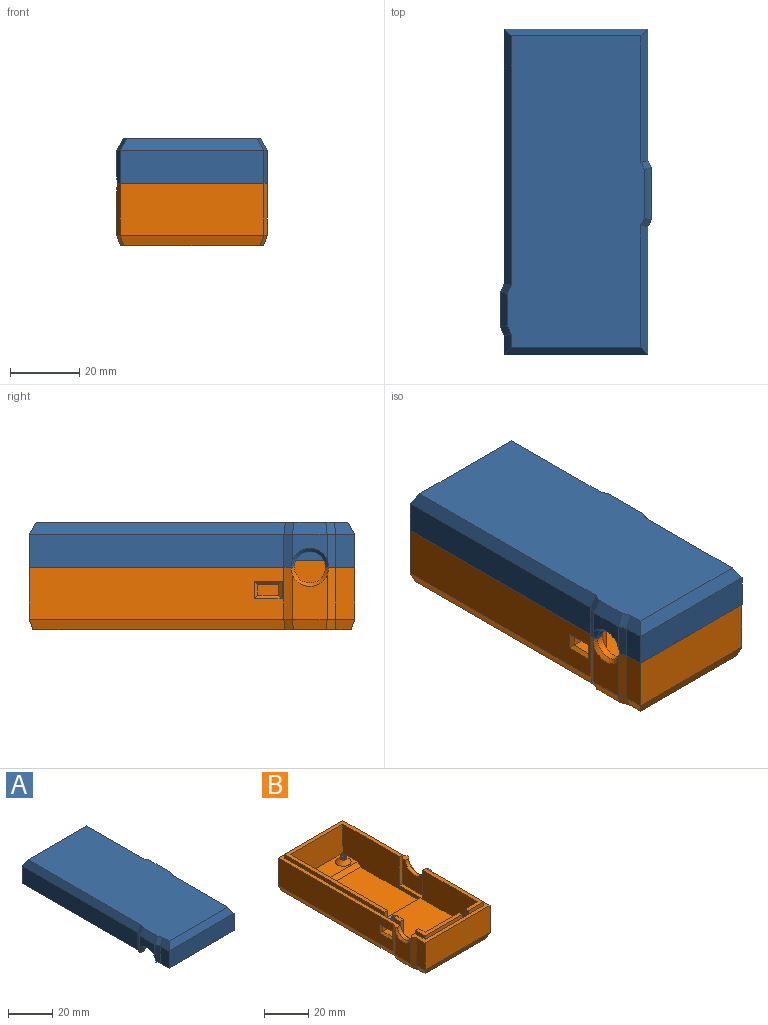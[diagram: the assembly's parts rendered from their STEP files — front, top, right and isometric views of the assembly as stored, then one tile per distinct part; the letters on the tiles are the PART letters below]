
ASSEMBLY  parts=2 mates=1
PART A: 69 faces, bbox 43.6x94.1x20.1 mm
  f0: plane 88x37.5mm, normal (0,0,-1), area 2730.7mm2, adj f15,f16,f17,f18,f19,f20,f21,f22
  f1: plane 37.5x6.43mm, normal (0,-1,0), area 110.4mm2, adj f2,f19,f23,f25,f29,f36,f37,f49
  f2: plane 76.5x43.36mm, normal (0,0,-1), area 315.8mm2, adj f1,f4,f6,f7,f8,f9,f10,f19
  f3: plane 10x7.24mm, normal (-1,0,0), area 49.4mm2, adj f10,f11,f62,f64
  f4: plane 15x9.54mm, normal (1,0,0), area 76.7mm2, adj f2,f5,f6,f31,f53,f68
  f5: plane 43.36x41mm, normal (0,0,-1), area 177.8mm2, adj f4,f11,f12,f13,f14,f19,f29,f31
  f6: plane 9.54x2mm, normal (0.89,0.45,0), area 21.3mm2, adj f2,f4,f7,f55
  f7: plane 38x9.54mm, normal (1,0,0), area 362.4mm2, adj f2,f6,f8,f57
  f8: plane 41.5x9.54mm, normal (0,1,0), area 354.7mm2, adj f2,f7,f9,f59,f65,f66,f67
  f9: plane 73.53x9.54mm, normal (-1,0,0), area 701.2mm2, adj f2,f8,f10,f61
  f10: plane 9.64x2.57mm, normal (-0.93,0.38,0), area 24.8mm2, adj f2,f3,f9,f63,f64
  f11: plane 9.64x2.57mm, normal (-0.93,-0.38,0), area 24.8mm2, adj f3,f5,f12,f60,f64
  f12: plane 9.54x5.53mm, normal (-1,0,0), area 52.7mm2, adj f5,f11,f13,f58
  f13: plane 41.5x9.54mm, normal (0,-1,0), area 395.7mm2, adj f5,f12,f14,f56
  f14: plane 37x9.54mm, normal (1,0,0), area 352.8mm2, adj f5,f13,f31,f54
  f15: plane 35x9mm, normal (-1,0,0), area 315mm2, adj f0,f16,f30,f35
  f16: plane 33.5x9mm, normal (0,1,0), area 301.5mm2, adj f0,f15,f17,f35
  f17: plane 9x4mm, normal (1,0,0), area 36mm2, adj f0,f16,f18,f35
  f18: plane 9x2mm, normal (0,1,0), area 18mm2, adj f0,f17,f19,f35
  f19: plane 90x11mm, normal (1,0,0), area 238.2mm2, adj f0,f1,f2,f5,f18,f20,f34,f35
  f20: plane 9x2mm, normal (0,-1,0), area 18mm2, adj f0,f19,f21,f37
  f21: plane 72x9mm, normal (1,0,0), area 648mm2, adj f0,f20,f22,f37
  f22: plane 9x7.75mm, normal (0,-1,0), area 69.8mm2, adj f0,f21,f23,f37
  f23: plane 9x3mm, normal (1,0,0), area 21.1mm2, adj f0,f1,f22,f24,f37,f48,f49,f65
  f24: plane 8x1.43mm, normal (0,-1,0), area 11.4mm2, adj f0,f23,f25,f48
  f25: plane 9x3mm, normal (-1,0,0), area 21.1mm2, adj f0,f1,f24,f26,f36,f48,f49,f67
  f26: plane 17.75x9mm, normal (0,-1,0), area 155.4mm2, adj f0,f25,f27,f32,f36,f51
  f27: plane 36x9mm, normal (-1,0,0), area 318mm2, adj f0,f26,f28,f32,f36,f51
  f28: plane 9x2mm, normal (0,-1,0), area 18mm2, adj f0,f27,f29,f36
  f29: plane 90x11mm, normal (-1,0,0), area 267.5mm2, adj f0,f1,f2,f5,f28,f30,f34,f35
  f30: plane 9x2mm, normal (0,1,0), area 18mm2, adj f0,f15,f29,f35
  f31: plane 9.54x2mm, normal (0.89,-0.45,0), area 21.3mm2, adj f4,f5,f14,f52
  f32: plane 1.43x1.33mm, normal (0,0,-1), area 0.9mm2, adj f26,f27,f51
  f33: plane 90x39.5mm, normal (0,0,1), area 3402.7mm2, adj f52,f53,f54,f55,f56,f57,f58,f59
  f34: plane 37.5x2mm, normal (0,1,0), area 75mm2, adj f5,f19,f29,f35
  f35: plane 37.5x37mm, normal (0,0,-1), area 153mm2, adj f15,f16,f17,f18,f19,f29,f30,f34
  f36: plane 38x19.75mm, normal (0,0,-1), area 111.5mm2, adj f1,f25,f26,f27,f28,f29
  f37: plane 74x9.75mm, normal (0,0,-1), area 163.5mm2, adj f1,f19,f20,f21,f22,f23
  f38: cylinder r=1mm len=18mm, axis (0,0,1), area 113.1mm2, adj f40,f41
  f39: cylinder r=3mm len=15mm, axis (0,0,1), area 282.7mm2, adj f40,f51
  f40: plane 6x6mm, normal (0,0,-1), area 25.1mm2, adj f38,f39
  f41: plane 2x2mm, normal (0,0,-1), area 3.1mm2, adj f38
  f42: cylinder r=1mm len=18mm, axis (0,0,1), area 113.1mm2, adj f44,f45
  f43: cylinder r=3mm len=15mm, axis (0,0,1), area 282.7mm2, adj f44,f50
  f44: plane 6x6mm, normal (0,0,-1), area 25.1mm2, adj f42,f43
  f45: plane 2x2mm, normal (0,0,-1), area 3.1mm2, adj f42
  f46: cylinder r=5.5mm len=11mm, axis (1,0,0), area 34.6mm2, adj f2,f5,f29,f68
  f47: cylinder r=4.5mm len=9mm, axis (-1,0,0), area 28.3mm2, adj f2,f5,f19,f64
  f48: plane 9.96x1.98mm, normal (0,0,-1), area 16.8mm2, adj f23,f24,f25,f59,f65,f67
  f49: plane 8x1mm, normal (0,0,1), area 8mm2, adj f1,f23,f25,f66
  f50: cone r=6mm half-angle=45deg, axis (0,0,1), area 120mm2, adj f0,f43
  f51: cone r=6mm half-angle=45deg, axis (0,0,1), area 104.8mm2, adj f0,f26,f27,f32,f39
  f52: plane 3.46x3mm, normal (0.77,-0.39,0.5), area 8.9mm2, adj f31,f33,f53,f54
  f53: plane 15x3.46mm, normal (0.87,0,0.5), area 58.1mm2, adj f4,f33,f52,f55
  f54: plane 37.47x3.46mm, normal (0.87,0,0.5), area 144.9mm2, adj f14,f33,f52,f56
  f55: plane 3.46x3mm, normal (0.77,0.39,0.5), area 8.9mm2, adj f6,f33,f53,f57
  f56: plane 41.5x3.46mm, normal (0,-0.87,0.5), area 158mm2, adj f13,f33,f54,f58
  f57: plane 38.47x3.46mm, normal (0.87,0,0.5), area 148.9mm2, adj f7,f33,f55,f59
  f58: plane 5.92x3.46mm, normal (-0.87,0,0.5), area 18.9mm2, adj f12,f33,f56,f60
  f59: plane 41.5x3.46mm, normal (0,0.87,0.5), area 157.6mm2, adj f8,f33,f48,f57,f61,f65,f67
  f60: plane 3.46x3mm, normal (-0.8,-0.32,0.5), area 10.7mm2, adj f11,f33,f58,f62
  f61: plane 73.92x3.46mm, normal (-0.87,0,0.5), area 290.9mm2, adj f9,f33,f59,f63
  f62: plane 10x3.46mm, normal (-0.87,0,0.5), area 38.4mm2, adj f3,f33,f60,f63
  f63: plane 3.46x3mm, normal (-0.8,0.32,0.5), area 10.7mm2, adj f10,f33,f61,f62
  f64: cone r=4.5mm half-angle=45deg, axis (-1,0,0), area 21.7mm2, adj f2,f3,f5,f10,f11,f47
  f65: plane 4.14x1mm, normal (0.71,0.71,0), area 5.2mm2, adj f8,f23,f48,f59,f66
  f66: plane 10x1mm, normal (0,0.71,0.71), area 12.7mm2, adj f8,f49,f65,f67
  f67: plane 4.14x1mm, normal (-0.71,0.71,0), area 5.2mm2, adj f8,f25,f48,f59,f66
  f68: cone r=5.5mm half-angle=45deg, axis (1,0,0), area 26.7mm2, adj f2,f4,f5,f46
PART B: 84 faces, bbox 43.5x94x20 mm
  f0: plane 35x16mm, normal (-1,0,0), area 560mm2, adj f9,f12,f13,f42
  f1: plane 4x2mm, normal (-1,0,0), area 8mm2, adj f2,f5,f21,f58
  f2: plane 4x2mm, normal (0,0,1), area 8mm2, adj f1,f3,f21,f58
  f3: plane 72x18mm, normal (1,0,0), area 1168mm2, adj f2,f7,f9,f21,f22,f39,f52,f56
  f4: plane 73.53x15mm, normal (-1,0,0), area 1062.9mm2, adj f5,f30,f31,f71,f72,f73,f74,f75
  f5: plane 76.5x43.36mm, normal (0,0,1), area 315.8mm2, adj f1,f4,f11,f20,f27,f28,f29,f30
  f6: plane 12.71x10mm, normal (-1,0,0), area 104mm2, adj f31,f32,f67,f77
  f7: plane 33.5x9.44mm, normal (0,0,1), area 277.6mm2, adj f3,f22,f23,f79,f81
  f8: plane 15x2mm, normal (0,0,1), area 30mm2, adj f9,f11,f12,f23,f34
  f9: plane 38.51x35.5mm, normal (0,0,1), area 1212.8mm2, adj f0,f3,f8,f13,f14,f15,f16,f17
  f10: plane 43.36x41mm, normal (0,0,1), area 177.8mm2, adj f11,f15,f20,f24,f25,f26,f27,f32
  f11: plane 15x14mm, normal (-1,0,0), area 162.5mm2, adj f5,f8,f10,f12,f34,f53
  f12: plane 16x2mm, normal (0,1,0), area 32mm2, adj f0,f8,f11,f41,f42
  f13: plane 16x7.72mm, normal (0,1,0), area 123.6mm2, adj f0,f9,f14,f42
  f14: plane 16x2mm, normal (-1,0,0), area 32mm2, adj f9,f13,f15,f40,f42
  f15: plane 14x4mm, normal (0,1,0), area 56mm2, adj f9,f10,f14,f16
  f16: plane 16x2mm, normal (1,0,0), area 32mm2, adj f9,f15,f17,f43,f45
  f17: plane 21.78x16mm, normal (0,1,0), area 348.4mm2, adj f9,f16,f18,f45
  f18: plane 16x4mm, normal (1,0,0), area 64mm2, adj f9,f17,f19,f45
  f19: plane 16x2mm, normal (0,1,0), area 32mm2, adj f9,f18,f20,f44,f45
  f20: plane 14x10mm, normal (1,0,0), area 108.2mm2, adj f5,f9,f10,f19,f21,f54
  f21: plane 16x2mm, normal (0,-1,0), area 32mm2, adj f1,f2,f3,f9,f20
  f22: plane 33.5x16mm, normal (0,-1,0), area 536mm2, adj f3,f7,f23,f39
  f23: plane 49.49x18mm, normal (-1,0,0), area 652.1mm2, adj f7,f8,f22,f34,f39,f52,f78,f79
  f24: plane 41.5x15mm, normal (0,-1,0), area 622.5mm2, adj f10,f25,f33,f61
  f25: plane 37x15mm, normal (1,0,0), area 555mm2, adj f10,f24,f26,f60
  f26: plane 15x2mm, normal (0.89,-0.45,0), area 33.5mm2, adj f10,f25,f27,f62
  f27: plane 15x15mm, normal (1,0,0), area 158.6mm2, adj f5,f10,f26,f28,f64,f76
  f28: plane 15x2mm, normal (0.89,0.45,0), area 33.5mm2, adj f5,f27,f29,f66
  f29: plane 38x15mm, normal (1,0,0), area 570mm2, adj f5,f28,f30,f68
  f30: plane 41.5x15mm, normal (0,1,0), area 622.5mm2, adj f4,f5,f29,f70
  f31: plane 15x2.47mm, normal (-0.93,0.38,0), area 39.4mm2, adj f4,f5,f6,f69,f77
  f32: plane 15x2.47mm, normal (-0.93,-0.38,0), area 39.4mm2, adj f6,f10,f33,f65,f77
  f33: plane 15x5.53mm, normal (-1,0,0), area 82.9mm2, adj f10,f24,f32,f63
  f34: plane 16x2mm, normal (0,-1,0), area 32mm2, adj f8,f11,f23,f36,f39
  f35: plane 91.82x41.32mm, normal (0,0,-1), area 3581.8mm2, adj f60,f61,f62,f63,f64,f65,f66,f67
  f36: plane 38x2mm, normal (1,0,0), area 76mm2, adj f5,f34,f37,f39
  f37: plane 37.5x2mm, normal (0,1,0), area 75mm2, adj f5,f36,f38,f39
  f38: plane 64x2mm, normal (-1,0,0), area 128mm2, adj f5,f37,f39,f56
  f39: plane 64x37.5mm, normal (0,0,1), area 271mm2, adj f3,f22,f23,f34,f36,f37,f38,f56
  f40: plane 9.72x2mm, normal (0,-1,0), area 19.4mm2, adj f10,f14,f41,f42
  f41: plane 37x2mm, normal (1,0,0), area 74mm2, adj f10,f12,f40,f42
  f42: plane 37x9.72mm, normal (0,0,1), area 89.4mm2, adj f0,f12,f13,f14,f40,f41
  f43: plane 23.78x2mm, normal (0,-1,0), area 47.6mm2, adj f10,f16,f44,f45
  f44: plane 6x2mm, normal (-1,0,0), area 12mm2, adj f10,f19,f43,f45
  f45: plane 23.78x6mm, normal (0,0,1), area 55.6mm2, adj f16,f17,f18,f19,f43,f44
  f46: cylinder r=1mm len=5mm, axis (0,0,1), area 31.4mm2, adj f51,f83
  f47: cylinder r=1mm len=5mm, axis (0,0,1), area 31.4mm2, adj f49,f82
  f48: cylinder r=1.5mm len=3mm, axis (0,0,-1), area 9.4mm2, adj f49,f81
  f49: plane 3x3mm, normal (0,0,1), area 3.9mm2, adj f47,f48
  f50: cylinder r=1.5mm len=3mm, axis (0,0,-1), area 9.4mm2, adj f51,f80
  f51: plane 3x3mm, normal (0,0,1), area 3.9mm2, adj f46,f50
  f52: plane 36.05x33.5mm, normal (0,0,1), area 1207.6mm2, adj f3,f23,f78,f79
  f53: cylinder r=5.5mm len=11mm, axis (1,0,0), area 34.6mm2, adj f5,f10,f11,f76
  f54: cylinder r=4.5mm len=9mm, axis (-1,0,0), area 28.3mm2, adj f5,f10,f20,f77
  f55: plane 6x1mm, normal (0,0,-1), area 6mm2, adj f56,f58,f59,f74
  f56: plane 10.02x3mm, normal (0,-1,0), area 23mm2, adj f3,f38,f39,f55,f57,f59,f72
  f57: plane 6x3mm, normal (0,0,1), area 18mm2, adj f3,f56,f58,f73
  f58: plane 10.02x3mm, normal (0,1,0), area 23mm2, adj f1,f2,f3,f55,f57,f59,f75
  f59: plane 6x5.02mm, normal (1,0,0), area 30.1mm2, adj f5,f55,f56,f58
  f60: plane 37.26x3mm, normal (0.94,0,-0.34), area 116.8mm2, adj f25,f35,f61,f62
  f61: plane 41.5x3mm, normal (0,-0.94,-0.34), area 129mm2, adj f24,f35,f60,f63
  f62: plane 3x2.26mm, normal (0.84,-0.42,-0.34), area 7.1mm2, adj f26,f35,f60,f64
  f63: plane 5.74x3mm, normal (-0.94,0,-0.34), area 16.2mm2, adj f33,f35,f61,f65
  f64: plane 15x3mm, normal (0.94,0,-0.34), area 47.1mm2, adj f27,f35,f62,f66
  f65: plane 3x2.68mm, normal (-0.87,-0.35,-0.34), area 8.5mm2, adj f32,f35,f63,f67
  f66: plane 3x2.26mm, normal (0.84,0.42,-0.34), area 7.1mm2, adj f28,f35,f64,f68
  f67: plane 10x3mm, normal (-0.94,0,-0.34), area 31.2mm2, adj f6,f35,f65,f69
  f68: plane 38.26x3mm, normal (0.94,0,-0.34), area 120mm2, adj f29,f35,f66,f70
  f69: plane 3x2.68mm, normal (-0.87,0.35,-0.34), area 8.5mm2, adj f31,f35,f67,f71
  f70: plane 41.5x3mm, normal (0,0.94,-0.34), area 129mm2, adj f30,f35,f68,f71
  f71: plane 73.74x3mm, normal (-0.94,0,-0.34), area 233.3mm2, adj f4,f35,f69,f70
  f72: plane 5x1mm, normal (-0.71,-0.71,0), area 5.7mm2, adj f4,f56,f73,f74
  f73: plane 8x1mm, normal (-0.71,0,0.71), area 9.9mm2, adj f4,f57,f72,f75
  f74: plane 8x1mm, normal (-0.71,0,-0.71), area 9.9mm2, adj f4,f55,f72,f75
  f75: plane 5x1mm, normal (-0.71,0.71,0), area 5.7mm2, adj f4,f58,f73,f74
  f76: cone r=5.5mm half-angle=45deg, axis (1,0,0), area 26.7mm2, adj f5,f10,f27,f53
  f77: cone r=4.5mm half-angle=45deg, axis (-1,0,0), area 21.6mm2, adj f5,f6,f10,f31,f32,f54
  f78: plane 33.5x2mm, normal (0,0.71,0.71), area 94.8mm2, adj f3,f9,f23,f52
  f79: plane 33.5x2mm, normal (0,-0.71,0.71), area 94.8mm2, adj f3,f7,f23,f52
  f80: cone r=1.5mm half-angle=45deg, axis (0,0,-1), area 44.4mm2, adj f9,f50
  f81: cone r=1.5mm half-angle=45deg, axis (0,0,-1), area 44.4mm2, adj f7,f48
  f82: cone r=1mm half-angle=45deg, axis (0,0,-1), area 35.5mm2, adj f35,f47
  f83: cone r=1mm half-angle=45deg, axis (0,0,-1), area 35.5mm2, adj f35,f46
PLACE A t=(0.03,0.32,18)mm
PLACE B t=(0.03,0.32,18)mm
MATE fastened B.f5 <-> A.f2  axis (0,0,1) through (20.78,47.32,18)mm
